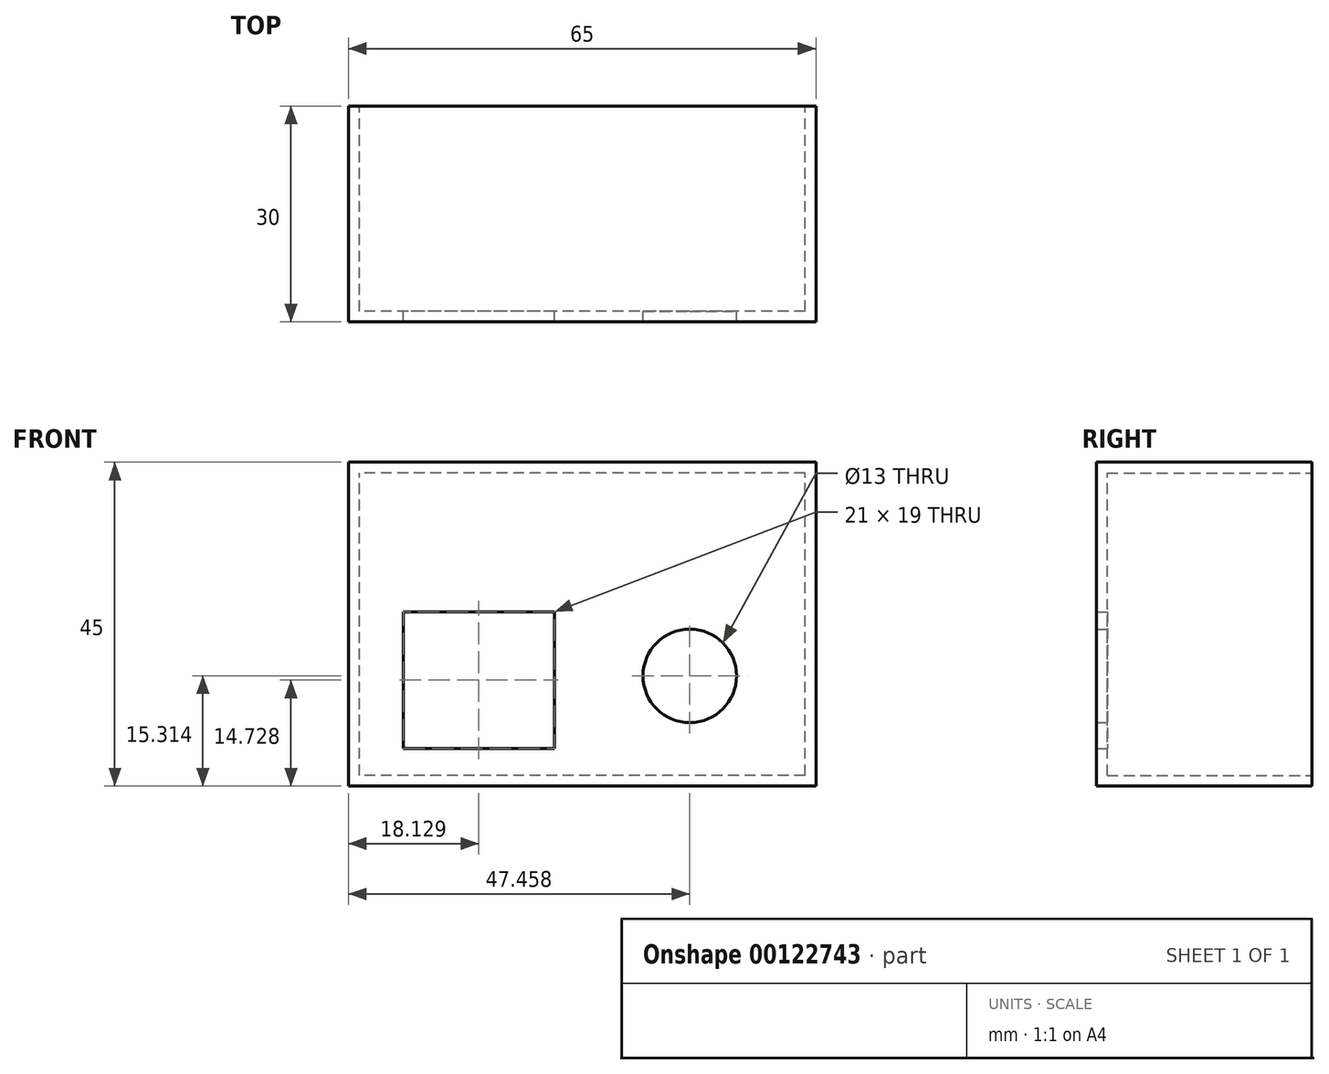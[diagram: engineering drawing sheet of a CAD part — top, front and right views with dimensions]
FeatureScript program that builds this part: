
annotation { "Feature Type Name" : "Feature", "Feature Type Description" : "" }
export const myFeature = defineFeature(function(context is Context, id is Id, definition is map)
    precondition{}
    {
        {
            var Q0;
            Q0=qCreatedBy(makeId("Front.planeOp"),FACE);
            var sketch = newSketch(context, id + "F0", { "sketchPlane" : qUnion([Q0])});
            skLineSegment(sketch, "E0.bottom", {"start": v(32.5, -22.5) * mm, "end": v(-32.5, -22.5) * mm});
            skLineSegment(sketch, "E0.top", {"start": v(32.5, 22.5) * mm, "end": v(-32.5, 22.5) * mm});
            skLineSegment(sketch, "E0.left", {"start": v(32.5, -22.5) * mm, "end": v(32.5, 22.5) * mm});
            skLineSegment(sketch, "E0.right", {"start": v(-32.5, -22.5) * mm, "end": v(-32.5, 22.5) * mm});
            skPoint(sketch, "E0.middle", {"position": v(0, 0) * mm});
            skLineSegment(sketch, "E1", {"start": v(-70.98, 7.5) * mm, "end": v(65.7, 7.5) * mm, "construction": true});
            skLineSegment(sketch, "E2.bottom", {"start": v(-3.87, 1.73) * mm, "end": v(-24.87, 1.73) * mm});
            skLineSegment(sketch, "E2.top", {"start": v(-3.87, -17.27) * mm, "end": v(-24.87, -17.27) * mm});
            skLineSegment(sketch, "E2.left", {"start": v(-3.87, 1.73) * mm, "end": v(-3.87, -17.27) * mm});
            skLineSegment(sketch, "E2.right", {"start": v(-24.87, 1.73) * mm, "end": v(-24.87, -17.27) * mm});
            skPoint(sketch, "E2.middle", {"position": v(-14.37, -7.77) * mm});
            skCircle(sketch, "E3", {"center": v(14.96, -7.19) * mm, "radius": 6.5 * mm});
            skSolve(sketch);
        }
        {
            var Q0;
            Q0 = qSketchRegion(id + "F0", true);
            extrude(context, id + "F1", {"entities" : qUnion([Q0]), "depth" : 30 * mm});
        }
        {
            var Q0;
            Q0=makeQuery(id+"F1.opExtrude","CAP_FACE",FACE,{"disambiguationData":[OSD([sQuery(id+"F0.wireOp",EDGE,"E0.bottom"),sQuery(id+"F0.wireOp",EDGE,"E0.top"),sQuery(id+"F0.wireOp",EDGE,"E0.left"),sQuery(id+"F0.wireOp",EDGE,"E0.right"),sQuery(id+"F0.wireOp",EDGE,"E2.bottom"),sQuery(id+"F0.wireOp",EDGE,"E2.top"),sQuery(id+"F0.wireOp",EDGE,"E2.left"),sQuery(id+"F0.wireOp",EDGE,"E2.right"),sQuery(id+"F0.wireOp",EDGE,"E3")])],"isStart":true});
            var Q1;
            Q1=makeQuery(id+"F1.opExtrude","SWEPT_FACE",FACE,{"disambiguationData":[OSD([sQuery(id+"F0.wireOp",EDGE,"E2.left")])]});
            var Q2;
            Q2=makeQuery(id+"F1.opExtrude","SWEPT_FACE",FACE,{"disambiguationData":[OSD([sQuery(id+"F0.wireOp",EDGE,"E3")])]});
            var Q3;
            Q3=makeQuery(id+"F1.opExtrude","SWEPT_FACE",FACE,{"disambiguationData":[OSD([sQuery(id+"F0.wireOp",EDGE,"E2.right")])]});
            var Q4;
            Q4=makeQuery(id+"F1.opExtrude","SWEPT_FACE",FACE,{"disambiguationData":[OSD([sQuery(id+"F0.wireOp",EDGE,"E2.bottom")])]});
            var Q5;
            Q5=makeQuery(id+"F1.opExtrude","SWEPT_FACE",FACE,{"disambiguationData":[OSD([sQuery(id+"F0.wireOp",EDGE,"E2.top")])]});
            shell(context, id + "F2", {"entities" : qUnion([Q0, Q1, Q2, Q3, Q4, Q5]), "thickness" : 1.5 * mm});
        }
    });
